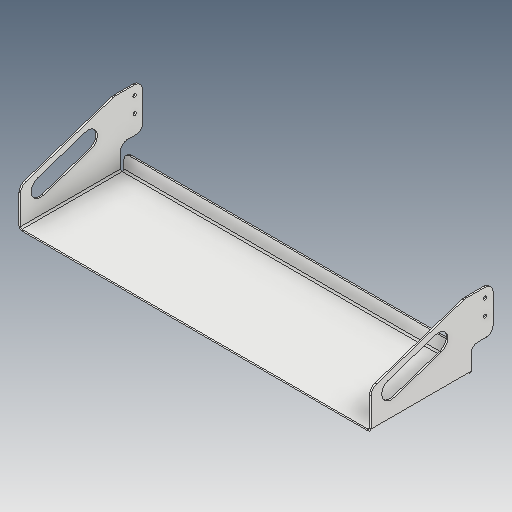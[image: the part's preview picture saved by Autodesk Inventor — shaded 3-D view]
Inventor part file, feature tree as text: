
AUTODESK INVENTOR PART (.ipt)
format: ipt  version: 2023.5 (Build 275446000, 446)  size: 143,360 bytes
history: native  units: in
note: dims shown in document units (in); Inventor stores cm internally (conversion verified against a paired STEP export)
features: fillet x1
ambient origin geometry x8: Origin, YZ Plane, XZ Plane, XY Plane, X Axis, Y Axis, Z Axis, Center Point
bodies: Solid1 (feature_tree)
feature tree (1):
  fillet  "Fillet2"  [1 undecoded]
note: 1 required parameter value undecoded (feature->parameter linkage not recoverable at this tier; creation-order binding heuristic only, values carry confidence <= 0.55)
